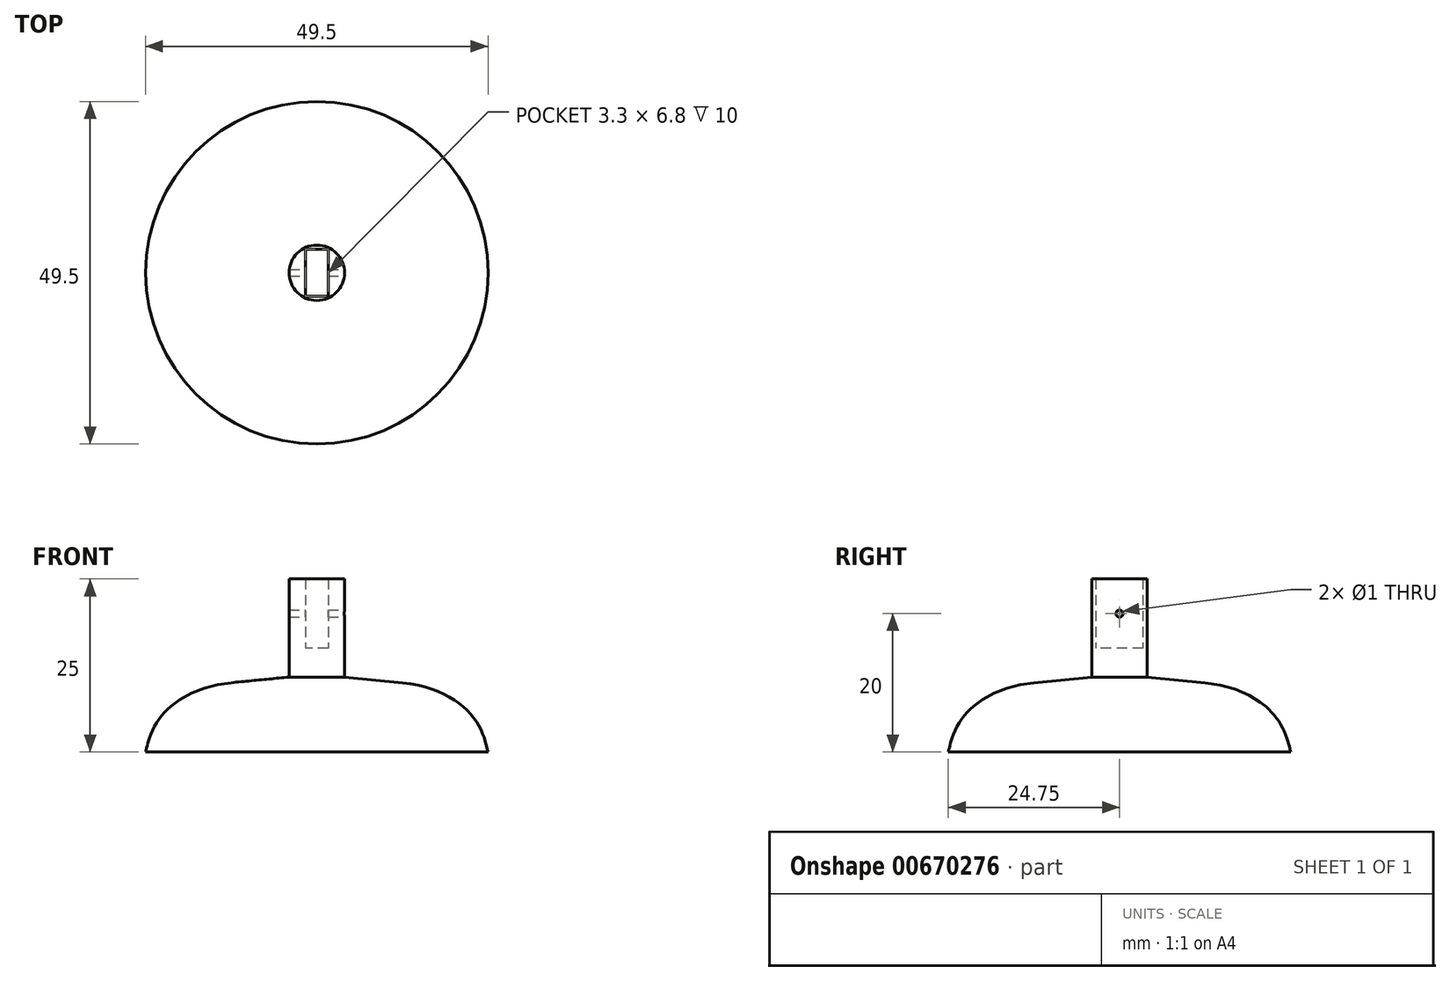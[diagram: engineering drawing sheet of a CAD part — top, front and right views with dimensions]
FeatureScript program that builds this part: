
annotation { "Feature Type Name" : "Feature", "Feature Type Description" : "" }
export const myFeature = defineFeature(function(context is Context, id is Id, definition is map)
    precondition{}
    {
        {
            var Q0;
            Q0=qCreatedBy(makeId("Top.planeOp"),FACE);
            var sketch = newSketch(context, id + "F0", { "sketchPlane" : qUnion([Q0])});
            skCircle(sketch, "E0", {"center": v(0, 0) * mm, "radius": 4 * mm});
            skCircle(sketch, "E1", {"center": v(0, 0) * mm, "radius": 25 * mm});
            skLineSegment(sketch, "E2.bottom", {"start": v(1.65, 3.4) * mm, "end": v(-1.65, 3.4) * mm});
            skLineSegment(sketch, "E2.top", {"start": v(1.65, -3.4) * mm, "end": v(-1.65, -3.4) * mm});
            skLineSegment(sketch, "E2.left", {"start": v(1.65, 3.4) * mm, "end": v(1.65, -3.4) * mm});
            skLineSegment(sketch, "E2.right", {"start": v(-1.65, 3.4) * mm, "end": v(-1.65, -3.4) * mm});
            skLineSegment(sketch, "E3", {"start": v(-1.65, 0) * mm, "end": v(1.65, 0) * mm});
            skSolve(sketch);
        }
        {
            var Q0;
            Q0=makeQuery(id+"F0.imprint","IMPRINT",FACE,{"disambiguationData":[TD([[makeQuery(id+"F0.imprint","IMPRINT",EDGE,{"derivedFrom":sQuery(id+"F0.wireOp",EDGE,"E0")}),1.0]])]});
            extrude(context, id + "F1", {"entities" : qUnion([Q0]), "depth" : 25 * mm, "offsetDistance" : 25 * mm});
        }
        {
            var Q0;
            Q0=qCreatedBy(makeId("Front.planeOp"),FACE);
            var sketch = newSketch(context, id + "F2", { "sketchPlane" : qUnion([Q0])});
            skLineSegment(sketch, "E4.bottom", {"start": v(0, 0) * mm, "end": v(-24.75, 0) * mm});
            skLineSegment(sketch, "E4.left", {"start": v(0, 0) * mm, "end": v(0, 10) * mm});
            skFitSpline(sketch, "E5", {"points": [v(-24.75, 0) * mm, v(-23.26, 4.08) * mm, v(-12.37, 10) * mm], "startDerivative": vector(1.56, 5.89) * mm, "endDerivative": vector(26.76, 2.65) * mm});
            skLineSegment(sketch, "E6", {"start": v(0, 10) * mm, "end": v(0, 35) * mm});
            skLineSegment(sketch, "E7", {"start": v(-12.37, 10) * mm, "end": v(0, 11.23) * mm});
            skSolve(sketch);
        }
        {
            var Q0;
            Q0=makeQuery(id+"F2.imprint","IMPRINT",FACE,{"disambiguationData":[TD([[makeQuery(id+"F2.imprint","IMPRINT",EDGE,{"derivedFrom":sQuery(id+"F2.wireOp",EDGE,"E4.bottom")}),-1.0]])]});
            var Q1;
            Q1=makeQuery(id+"F1.opExtrude","SWEPT_FACE",FACE,{"disambiguationData":[OSD([sQuery(id+"F0.wireOp",EDGE,"E0")])]});
            revolve(context, id + "F3", {"operationType" : NewBodyOperationType.ADD, "entities" : qUnion([Q0]), "axis" : qUnion([Q1]), "revolveType" : RevolveType.FULL});
        }
        {
            var Q0;
            Q0=makeQuery(id+"F0.imprint","IMPRINT",FACE,{"disambiguationData":[TD([[makeQuery(id+"F0.imprint","IMPRINT",EDGE,{"derivedFrom":sQuery(id+"F0.wireOp",EDGE,"E2.bottom")}),1.0]])]});
            var Q1;
            {var subQ0=sQuery(id+"F0.wireOp",EDGE,"E2.top");Q1=makeQuery(id+"F0.imprint","IMPRINT",FACE,{"disambiguationData":[TD([[makeQuery(id+"F0.imprint","IMPRINT",EDGE,{"derivedFrom":subQ0}),-1.0]])]});}
            extrude(context, id + "F4", {"entities" : qUnion([Q0, Q1]), "operationType" : NewBodyOperationType.ADD, "depth" : 15 * mm, "offsetDistance" : 25 * mm});
        }
        {
            var Q0;
            Q0=makeQuery(id+"F1.opExtrude","SWEPT_FACE",FACE,{"disambiguationData":[OSD([sQuery(id+"F0.wireOp",EDGE,"E2.left")])]});
            var sketch = newSketch(context, id + "F5", { "sketchPlane" : qUnion([Q0])});
            skCircle(sketch, "E8", {"center": v(0, 20) * mm, "radius": 0.5 * mm});
            skPoint(sketch, "E8.centerSnap0", {"position": v(3.4, 20) * mm});
            skPoint(sketch, "E8.centerSnap1", {"position": v(0, 15) * mm});
            skSolve(sketch);
        }
        {
            var Q0;
            Q0 = qSketchRegion(id + "F5", true);
            extrude(context, id + "F6", {"entities" : qUnion([Q0]), "operationType" : NewBodyOperationType.REMOVE, "endBound" : BoundingType.THROUGH_ALL, "depth" : 25 * mm, "offsetDistance" : 25 * mm, "hasSecondDirection" : true, "secondDirectionOppositeDirection" : true, "secondDirectionDepth" : 25 * mm});
        }
    });
